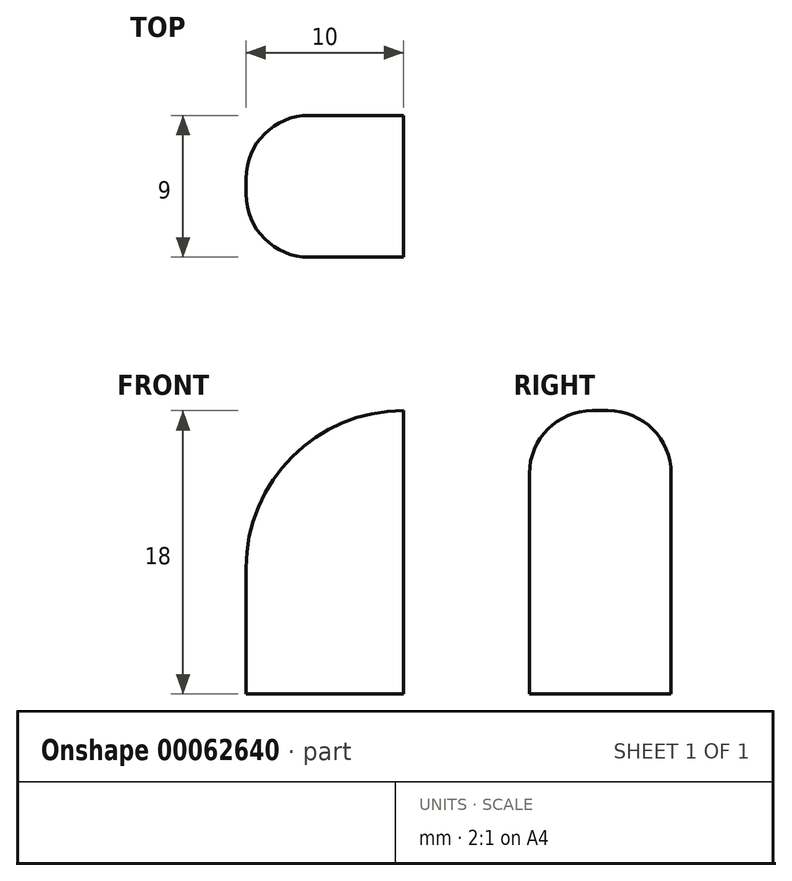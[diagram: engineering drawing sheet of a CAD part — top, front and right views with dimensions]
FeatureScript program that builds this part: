
annotation { "Feature Type Name" : "Feature", "Feature Type Description" : "" }
export const myFeature = defineFeature(function(context is Context, id is Id, definition is map)
    precondition{}
    {
        {
            var Q0;
            Q0=qCreatedBy(makeId("Front.planeOp"),FACE);
            var sketch = newSketch(context, id + "F0", { "sketchPlane" : qUnion([Q0])});
            skLineSegment(sketch, "E0", {"start": v(-10, 0) * mm, "end": v(0, 0) * mm});
            skLineSegment(sketch, "E1", {"start": v(0, 0) * mm, "end": v(0, 18) * mm});
            skLineSegment(sketch, "E2", {"start": v(-10, 8) * mm, "end": v(-10, 0) * mm});
            skArc(sketch, "E3", {"start": v(0, 18) * mm, "mid": v(-7.07, 15.07) * mm, "end": v(-10, 8) * mm});
            skSolve(sketch);
        }
        {
            var Q0;
            Q0 = qSketchRegion(id + "F0", true);
            extrude(context, id + "F1", {"entities" : qUnion([Q0]), "depth" : 9 * mm});
        }
        {
            var Q0;
            Q0=makeQuery(id+"F1.opExtrude","CAP_EDGE",EDGE,{"disambiguationData":[OSD([sQuery(id+"F0.wireOp",EDGE,"E3")])],"isStart":true});
            var Q1;
            Q1=makeQuery(id+"F1.opExtrude","CAP_EDGE",EDGE,{"disambiguationData":[OSD([sQuery(id+"F0.wireOp",EDGE,"E2")])],"isStart":true});
            var Q2;
            Q2=makeQuery(id+"F1.opExtrude","CAP_EDGE",EDGE,{"disambiguationData":[OSD([sQuery(id+"F0.wireOp",EDGE,"E2")])],"isStart":false});
            var Q3;
            Q3=makeQuery(id+"F1.opExtrude","CAP_EDGE",EDGE,{"disambiguationData":[OSD([sQuery(id+"F0.wireOp",EDGE,"E3")])],"isStart":false});
            fillet(context, id + "F2", {"entities" : qUnion([Q0, Q1, Q2, Q3]), "radius" : 4 * mm, "tangentPropagation" : true, "allowEdgeOverflow" : false});
        }
    });
